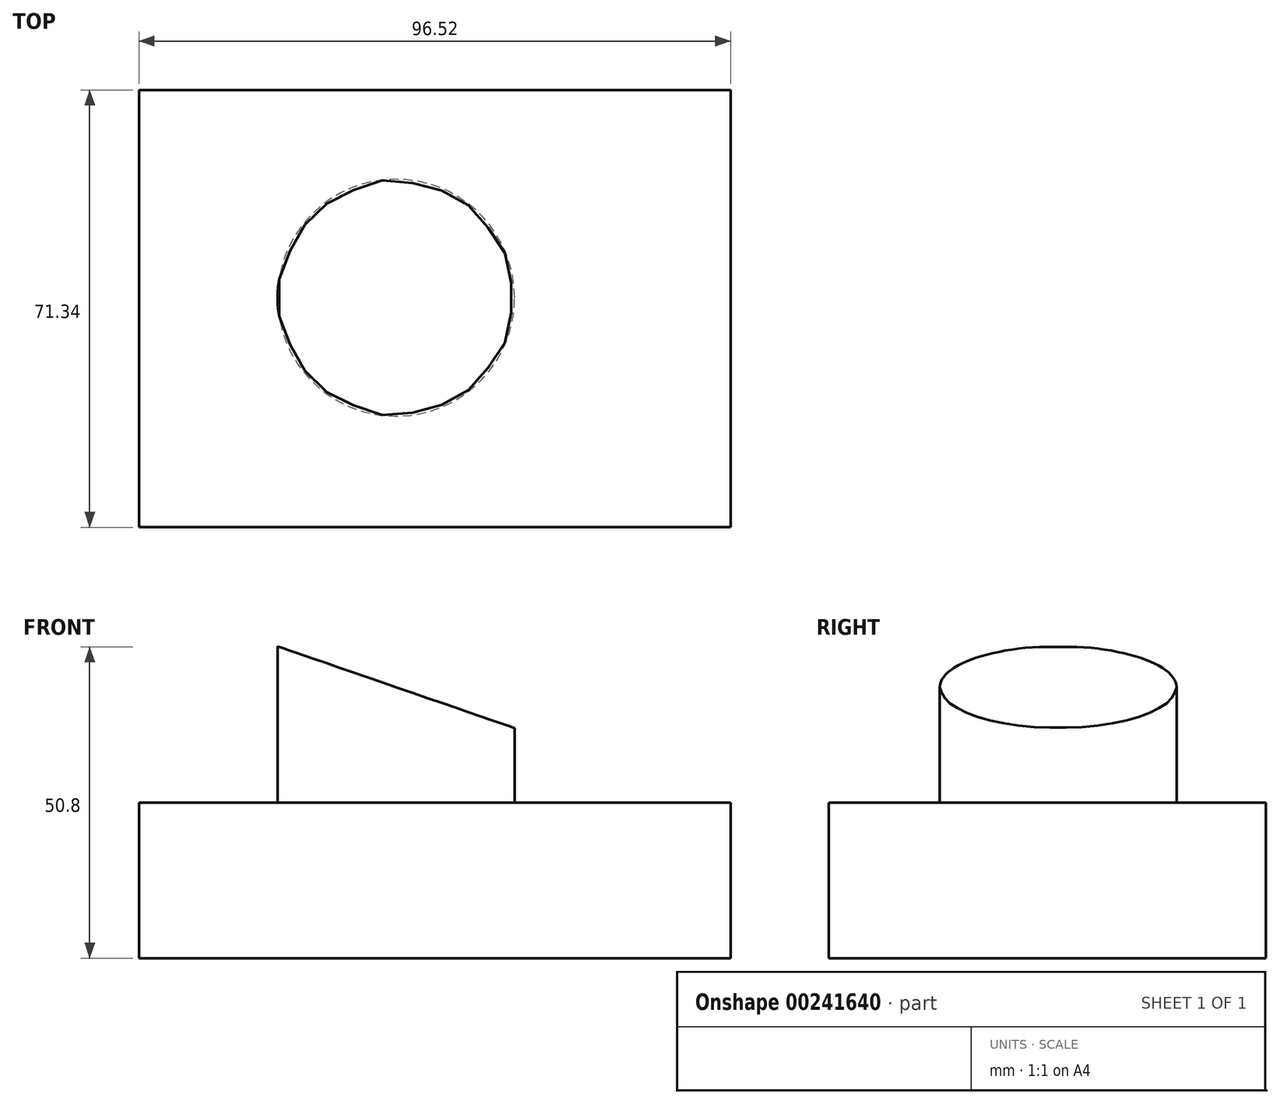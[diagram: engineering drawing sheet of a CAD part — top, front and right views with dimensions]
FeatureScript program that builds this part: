
annotation { "Feature Type Name" : "Feature", "Feature Type Description" : "" }
export const myFeature = defineFeature(function(context is Context, id is Id, definition is map)
    precondition{}
    {
        {
            var Q0;
            Q0=qCreatedBy(makeId("Top.planeOp"),FACE);
            var sketch = newSketch(context, id + "F0", { "sketchPlane" : qUnion([Q0])});
            skLineSegment(sketch, "E0", {"start": v(-41.95, 33.88) * mm, "end": v(54.57, 33.88) * mm});
            skLineSegment(sketch, "E1", {"start": v(54.57, -37.46) * mm, "end": v(54.57, 33.88) * mm});
            skLineSegment(sketch, "E2", {"start": v(54.57, -37.46) * mm, "end": v(-41.95, -37.46) * mm});
            skLineSegment(sketch, "E3", {"start": v(-41.95, -37.46) * mm, "end": v(-41.95, 33.88) * mm});
            skSolve(sketch);
        }
        {
            var Q0;
            Q0 = qSketchRegion(id + "F0", true);
            extrude(context, id + "F1", {"entities" : qUnion([Q0]), "depth" : 25.4 * mm});
        }
        {
            var Q0;
            Q0=makeQuery(id+"F1.opExtrude","CAP_FACE",FACE,{"disambiguationData":[OSD([sQuery(id+"F0.wireOp",EDGE,"E0"),sQuery(id+"F0.wireOp",EDGE,"E1"),sQuery(id+"F0.wireOp",EDGE,"E2"),sQuery(id+"F0.wireOp",EDGE,"E3")])],"isStart":false});
            var sketch = newSketch(context, id + "F2", { "sketchPlane" : qUnion([Q0])});
            skCircle(sketch, "E4", {"center": v(0, 0) * mm, "radius": 19.33 * mm});
            skSolve(sketch);
        }
        {
            var Q0;
            Q0=makeQuery(id+"F2.imprint","IMPRINT",FACE,{"disambiguationData":[TD([[makeQuery(id+"F2.imprint","IMPRINT",EDGE,{"derivedFrom":sQuery(id+"F2.wireOp",EDGE,"E4")}),1.0]])]});
            extrude(context, id + "F3", {"entities" : qUnion([Q0]), "operationType" : NewBodyOperationType.ADD, "depth" : 25.4 * mm});
        }
        {
            var Q0;
            Q0=makeQuery(id+"F1.opExtrude","SWEPT_FACE",FACE,{"disambiguationData":[OSD([sQuery(id+"F0.wireOp",EDGE,"E2")])]});
            var sketch = newSketch(context, id + "F4", { "sketchPlane" : qUnion([Q0])});
            skLineSegment(sketch, "E5", {"start": v(54.57, 25.4) * mm, "end": v(-20.25, 51.2) * mm});
            skLineSegment(sketch, "E6", {"start": v(-20.25, 51.2) * mm, "end": v(54.57, 51.2) * mm});
            skLineSegment(sketch, "E7", {"start": v(54.57, 51.2) * mm, "end": v(54.57, 25.4) * mm});
            skSolve(sketch);
        }
        {
            var Q0;
            Q0=makeQuery(id+"F4.imprint","IMPRINT",FACE,{"disambiguationData":[TD([[makeQuery(id+"F4.imprint","IMPRINT",EDGE,{"derivedFrom":sQuery(id+"F4.wireOp",EDGE,"E5")}),-1.0]])]});
            extrude(context, id + "F5", {"entities" : qUnion([Q0]), "operationType" : NewBodyOperationType.REMOVE, "endBound" : BoundingType.THROUGH_ALL, "oppositeDirection" : true, "depth" : 25.4 * mm});
        }
    });
